# Revit family: ASL_92_Series_timber_door_50mm_jamb_2
name_source: partatom
category: Detail Items
revit_build: Autodesk Revit 2018 (Build: 20170223_1515(x64)
units: mm (PartAtom-declared; Revit-internal decimal feet)

## family parameters
Rotate with component = No
Section Shape = Not Defined
Shared = Yes

## types (3) — shared parameters
Manufacturer = Aluminate Solutions Limited
Technical Info = www.aluminate.nz

## per-type parameters (varying)
| type | Door Depth | Door Stop | Door_50 | Flush Infill | Glazing | Type Comments |
| Double Action Door 50mm | 20 mm  [stored 0.0656168 ft] | No | Yes | Yes | No | ASL 92 Series Jamb 2 With Double Action 50mm Timber Door |
| Single Action Door 50mm | 72 mm  [stored 0.23622 ft] | Yes | Yes | No | No | ASL 92 Series Jamb 2 With Single Action 50mm Timber Door |
| Glazing | 20 mm  [stored 0.0656168 ft] | No | No | No | Yes | ASL 92 Series Jamb 2 With Glazing |

note: [stored X ft] marks values corroborated as IEEE doubles in the binary element streams (Revit-internal decimal feet)

## geometry (parser evidence)
native form markers: Sweep x8
no freeform markers — native parametric forms only
